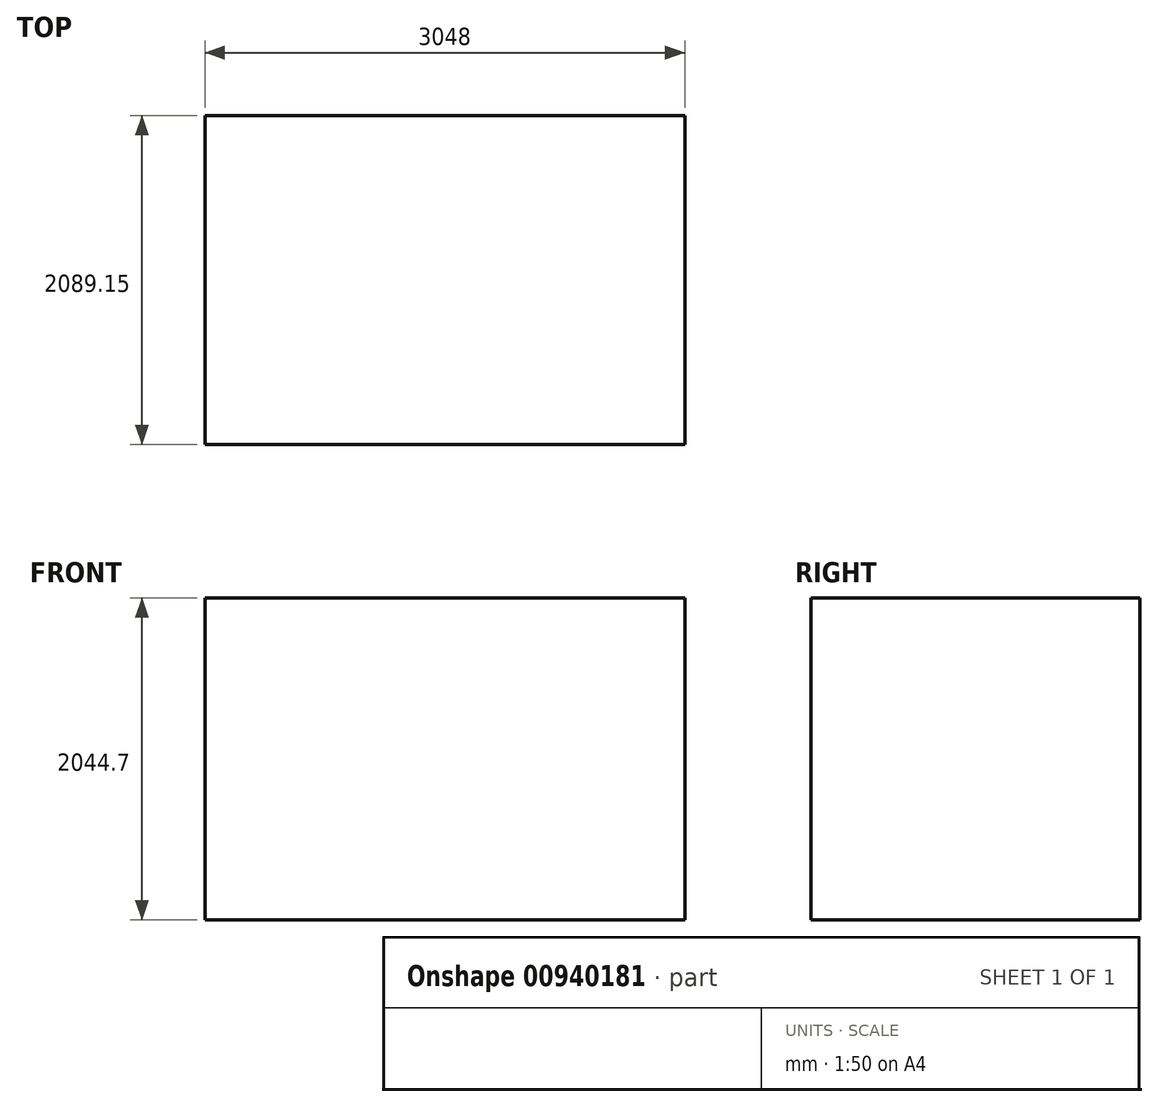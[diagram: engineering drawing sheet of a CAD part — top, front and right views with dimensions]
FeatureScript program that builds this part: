
annotation { "Feature Type Name" : "Feature", "Feature Type Description" : "" }
export const myFeature = defineFeature(function(context is Context, id is Id, definition is map)
    precondition{}
    {
        {
            var Q0;
            Q0=qCreatedBy(makeId("Front.planeOp"),FACE);
            var sketch = newSketch(context, id + "F0", { "sketchPlane" : qUnion([Q0])});
            skLineSegment(sketch, "E0.bottom", {"start": v(-1524, -1022.35) * mm, "end": v(1524, -1022.35) * mm});
            skLineSegment(sketch, "E0.top", {"start": v(-1524, 1022.35) * mm, "end": v(1524, 1022.35) * mm});
            skLineSegment(sketch, "E0.left", {"start": v(-1524, -1022.35) * mm, "end": v(-1524, 1022.35) * mm});
            skLineSegment(sketch, "E0.right", {"start": v(1524, -1022.35) * mm, "end": v(1524, 1022.35) * mm});
            skPoint(sketch, "E0.middle", {"position": v(0, 0) * mm});
            skLineSegment(sketch, "E1.bottom", {"start": v(-1200.05, 668.02) * mm, "end": v(-658.35, 668.02) * mm});
            skLineSegment(sketch, "E1.top", {"start": v(-1200.05, 161.65) * mm, "end": v(-658.35, 161.65) * mm});
            skLineSegment(sketch, "E1.left", {"start": v(-1200.05, 668.02) * mm, "end": v(-1200.05, 161.65) * mm});
            skLineSegment(sketch, "E1.right", {"start": v(-658.35, 668.02) * mm, "end": v(-658.35, 161.65) * mm});
            skLineSegment(sketch, "E2.bottom", {"start": v(478.03, 556.15) * mm, "end": v(1243.47, 556.15) * mm});
            skLineSegment(sketch, "E2.top", {"start": v(478.03, 0) * mm, "end": v(1243.47, 0) * mm});
            skLineSegment(sketch, "E2.left", {"start": v(478.03, 556.15) * mm, "end": v(478.03, 0) * mm});
            skLineSegment(sketch, "E2.right", {"start": v(1243.47, 556.15) * mm, "end": v(1243.47, 0) * mm});
            skLineSegment(sketch, "E3.bottom", {"start": v(354.38, -344.72) * mm, "end": v(1367.12, -344.72) * mm});
            skLineSegment(sketch, "E3.top", {"start": v(354.38, -939.4) * mm, "end": v(1367.12, -939.4) * mm});
            skLineSegment(sketch, "E3.left", {"start": v(354.38, -344.72) * mm, "end": v(354.38, -939.4) * mm});
            skLineSegment(sketch, "E3.right", {"start": v(1367.12, -344.72) * mm, "end": v(1367.12, -939.4) * mm});
            skText(sketch, "E4", { "text": "microwave", "fontName": "OpenSans-Regular.ttf"});
            skPoint(sketch, "E5", {"position": v(860.75, -344.72) * mm});
            skLineSegment(sketch, "E6", {"start": v(860.75, -344.72) * mm, "end": v(860.75, 1191.32) * mm, "construction": true});
            skPoint(sketch, "E7", {"position": v(860.75, 556.15) * mm});
            skText(sketch, "E8", { "text": "back wall", "fontName": "OpenSans-Regular.ttf"});
            skText(sketch, "E9", { "text": "window", "fontName": "OpenSans-Regular.ttf"});
            skText(sketch, "E10", { "text": "oven", "fontName": "OpenSans-Regular.ttf"});
            const initialGuessF0  = {"E4": [0.64839, 0.26293, 1, 0, 0.06366], "E8": [-0.68602, -0.1729, 1, 0, 0.0863], "E9": [-1.08292, 0.38795, 1, 0, 0.07798], "E10": [0.65703, -0.70805, 1, 0, 0.08726]};
            skSetInitialGuess(sketch, initialGuessF0);
            skSolve(sketch);
        }
        {
            var Q0;
            Q0 = qSketchRegion(id + "F0", true);
            var Q1;
            Q1=makeQuery(id+"F0.imprint","IMPRINT",FACE,{"disambiguationData":[TD([[makeQuery(id+"F0.imprint","IMPRINT",EDGE,{"derivedFrom":sQuery(id+"F0.wireOp",EDGE,"E8.sketch_text.stroke-122")}),1.0]])]});
            var Q2;
            Q2=makeQuery(id+"F0.imprint","IMPRINT",FACE,{"disambiguationData":[TD([[makeQuery(id+"F0.imprint","IMPRINT",EDGE,{"derivedFrom":sQuery(id+"F0.wireOp",EDGE,"E8.sketch_text.stroke-65")}),-1.0]])]});
            var Q3;
            Q3=makeQuery(id+"F0.imprint","IMPRINT",FACE,{"disambiguationData":[TD([[makeQuery(id+"F0.imprint","IMPRINT",EDGE,{"derivedFrom":sQuery(id+"F0.wireOp",EDGE,"E8.sketch_text.stroke-80")}),-1.0]])]});
            var Q4;
            Q4=makeQuery(id+"F0.imprint","IMPRINT",FACE,{"disambiguationData":[TD([[makeQuery(id+"F0.imprint","IMPRINT",EDGE,{"derivedFrom":sQuery(id+"F0.wireOp",EDGE,"E4.sketch_text.stroke-77")}),1.0]])]});
            var Q5;
            Q5=makeQuery(id+"F0.imprint","IMPRINT",FACE,{"disambiguationData":[TD([[makeQuery(id+"F0.imprint","IMPRINT",EDGE,{"derivedFrom":sQuery(id+"F0.wireOp",EDGE,"E4.sketch_text.stroke-127")}),1.0]])]});
            var Q6;
            Q6=makeQuery(id+"F0.imprint","IMPRINT",FACE,{"disambiguationData":[TD([[makeQuery(id+"F0.imprint","IMPRINT",EDGE,{"derivedFrom":sQuery(id+"F0.wireOp",EDGE,"E8.sketch_text.stroke-15")}),1.0]])]});
            var Q7;
            Q7=makeQuery(id+"F0.imprint","IMPRINT",FACE,{"disambiguationData":[TD([[makeQuery(id+"F0.imprint","IMPRINT",EDGE,{"derivedFrom":sQuery(id+"F0.wireOp",EDGE,"E8.sketch_text.stroke-42")}),1.0]])]});
            var Q8;
            Q8=makeQuery(id+"F0.imprint","IMPRINT",FACE,{"disambiguationData":[TD([[makeQuery(id+"F0.imprint","IMPRINT",EDGE,{"derivedFrom":sQuery(id+"F0.wireOp",EDGE,"E8.sketch_text.stroke-0")}),-1.0]])]});
            var Q9;
            Q9=makeQuery(id+"F0.imprint","IMPRINT",FACE,{"disambiguationData":[TD([[makeQuery(id+"F0.imprint","IMPRINT",EDGE,{"derivedFrom":sQuery(id+"F0.wireOp",EDGE,"E8.sketch_text.stroke-134")}),-1.0]])]});
            var Q10;
            Q10=makeQuery(id+"F0.imprint","IMPRINT",FACE,{"disambiguationData":[TD([[makeQuery(id+"F0.imprint","IMPRINT",EDGE,{"derivedFrom":sQuery(id+"F0.wireOp",EDGE,"E10.sketch_text.stroke-0")}),-1.0]])]});
            var Q11;
            Q11=makeQuery(id+"F0.imprint","IMPRINT",FACE,{"disambiguationData":[TD([[makeQuery(id+"F0.imprint","IMPRINT",EDGE,{"derivedFrom":sQuery(id+"F0.wireOp",EDGE,"E9.sketch_text.stroke-67")}),1.0]])]});
            var Q12;
            Q12=makeQuery(id+"F0.imprint","IMPRINT",FACE,{"disambiguationData":[TD([[makeQuery(id+"F0.imprint","IMPRINT",EDGE,{"derivedFrom":sQuery(id+"F0.wireOp",EDGE,"E9.sketch_text.stroke-85")}),1.0]])]});
            var Q13;
            Q13=makeQuery(id+"F0.imprint","IMPRINT",FACE,{"disambiguationData":[TD([[makeQuery(id+"F0.imprint","IMPRINT",EDGE,{"derivedFrom":sQuery(id+"F0.wireOp",EDGE,"E3.bottom")}),-1.0]])]});
            var Q14;
            Q14=makeQuery(id+"F0.imprint","IMPRINT",FACE,{"disambiguationData":[TD([[makeQuery(id+"F0.imprint","IMPRINT",EDGE,{"derivedFrom":sQuery(id+"F0.wireOp",EDGE,"E1.bottom")}),-1.0]])]});
            var Q15;
            Q15=makeQuery(id+"F0.imprint","IMPRINT",FACE,{"disambiguationData":[TD([[makeQuery(id+"F0.imprint","IMPRINT",EDGE,{"derivedFrom":sQuery(id+"F0.wireOp",EDGE,"E10.sketch_text.stroke-9")}),1.0]])]});
            var Q16;
            Q16=makeQuery(id+"F0.imprint","IMPRINT",FACE,{"disambiguationData":[TD([[makeQuery(id+"F0.imprint","IMPRINT",EDGE,{"derivedFrom":sQuery(id+"F0.wireOp",EDGE,"E0.bottom")}),1.0]])]});
            var Q17;
            Q17=makeQuery(id+"F0.imprint","IMPRINT",FACE,{"disambiguationData":[TD([[makeQuery(id+"F0.imprint","IMPRINT",EDGE,{"derivedFrom":sQuery(id+"F0.wireOp",EDGE,"E2.bottom")}),-1.0]])]});
            var Q18;
            Q18=makeQuery(id+"F0.imprint","IMPRINT",FACE,{"disambiguationData":[TD([[makeQuery(id+"F0.imprint","IMPRINT",EDGE,{"derivedFrom":sQuery(id+"F0.wireOp",EDGE,"E10.sketch_text.stroke-41")}),1.0]])]});
            var Q19;
            Q19=makeQuery(id+"F0.imprint","IMPRINT",FACE,{"disambiguationData":[TD([[makeQuery(id+"F0.imprint","IMPRINT",EDGE,{"derivedFrom":sQuery(id+"F0.wireOp",EDGE,"E4.sketch_text.stroke-0")}),-1.0]])]});
            var Q20;
            Q20=makeQuery(id+"F0.imprint","IMPRINT",FACE,{"disambiguationData":[TD([[makeQuery(id+"F0.imprint","IMPRINT",EDGE,{"derivedFrom":sQuery(id+"F0.wireOp",EDGE,"E4.sketch_text.stroke-28")}),-1.0]])]});
            var Q21;
            Q21=makeQuery(id+"F0.imprint","IMPRINT",FACE,{"disambiguationData":[TD([[makeQuery(id+"F0.imprint","IMPRINT",EDGE,{"derivedFrom":sQuery(id+"F0.wireOp",EDGE,"E4.sketch_text.stroke-40")}),-1.0]])]});
            var Q22;
            Q22=makeQuery(id+"F0.imprint","IMPRINT",FACE,{"disambiguationData":[TD([[makeQuery(id+"F0.imprint","IMPRINT",EDGE,{"derivedFrom":sQuery(id+"F0.wireOp",EDGE,"E4.sketch_text.stroke-55")}),-1.0]])]});
            var Q23;
            Q23=makeQuery(id+"F0.imprint","IMPRINT",FACE,{"disambiguationData":[TD([[makeQuery(id+"F0.imprint","IMPRINT",EDGE,{"derivedFrom":sQuery(id+"F0.wireOp",EDGE,"E4.sketch_text.stroke-85")}),-1.0]])]});
            var Q24;
            Q24=makeQuery(id+"F0.imprint","IMPRINT",FACE,{"disambiguationData":[TD([[makeQuery(id+"F0.imprint","IMPRINT",EDGE,{"derivedFrom":sQuery(id+"F0.wireOp",EDGE,"E4.sketch_text.stroke-135")}),-1.0]])]});
            var Q25;
            Q25=makeQuery(id+"F0.imprint","IMPRINT",FACE,{"disambiguationData":[TD([[makeQuery(id+"F0.imprint","IMPRINT",EDGE,{"derivedFrom":sQuery(id+"F0.wireOp",EDGE,"E4.sketch_text.stroke-159")}),1.0]])]});
            var Q26;
            Q26=makeQuery(id+"F0.imprint","IMPRINT",FACE,{"disambiguationData":[TD([[makeQuery(id+"F0.imprint","IMPRINT",EDGE,{"derivedFrom":sQuery(id+"F0.wireOp",EDGE,"E8.sketch_text.stroke-50")}),-1.0]])]});
            var Q27;
            Q27=makeQuery(id+"F0.imprint","IMPRINT",FACE,{"disambiguationData":[TD([[makeQuery(id+"F0.imprint","IMPRINT",EDGE,{"derivedFrom":sQuery(id+"F0.wireOp",EDGE,"E4.sketch_text.stroke-145")}),-1.0]])]});
            var Q28;
            Q28=makeQuery(id+"F0.imprint","IMPRINT",FACE,{"disambiguationData":[TD([[makeQuery(id+"F0.imprint","IMPRINT",EDGE,{"derivedFrom":sQuery(id+"F0.wireOp",EDGE,"E4.sketch_text.stroke-68")}),-1.0]])]});
            var Q29;
            Q29=makeQuery(id+"F0.imprint","IMPRINT",FACE,{"disambiguationData":[TD([[makeQuery(id+"F0.imprint","IMPRINT",EDGE,{"derivedFrom":sQuery(id+"F0.wireOp",EDGE,"E4.sketch_text.stroke-108")}),-1.0]])]});
            var Q30;
            Q30=makeQuery(id+"F0.imprint","IMPRINT",FACE,{"disambiguationData":[TD([[makeQuery(id+"F0.imprint","IMPRINT",EDGE,{"derivedFrom":sQuery(id+"F0.wireOp",EDGE,"E8.sketch_text.stroke-130")}),-1.0]])]});
            var Q31;
            Q31=makeQuery(id+"F0.imprint","IMPRINT",FACE,{"disambiguationData":[TD([[makeQuery(id+"F0.imprint","IMPRINT",EDGE,{"derivedFrom":sQuery(id+"F0.wireOp",EDGE,"E8.sketch_text.stroke-23")}),-1.0]])]});
            var Q32;
            Q32=makeQuery(id+"F0.imprint","IMPRINT",FACE,{"disambiguationData":[TD([[makeQuery(id+"F0.imprint","IMPRINT",EDGE,{"derivedFrom":sQuery(id+"F0.wireOp",EDGE,"E9.sketch_text.stroke-0")}),-1.0]])]});
            var Q33;
            Q33=makeQuery(id+"F0.imprint","IMPRINT",FACE,{"disambiguationData":[TD([[makeQuery(id+"F0.imprint","IMPRINT",EDGE,{"derivedFrom":sQuery(id+"F0.wireOp",EDGE,"E8.sketch_text.stroke-103")}),-1.0]])]});
            var Q34;
            Q34=makeQuery(id+"F0.imprint","IMPRINT",FACE,{"disambiguationData":[TD([[makeQuery(id+"F0.imprint","IMPRINT",EDGE,{"derivedFrom":sQuery(id+"F0.wireOp",EDGE,"E9.sketch_text.stroke-23")}),-1.0]])]});
            var Q35;
            Q35=makeQuery(id+"F0.imprint","IMPRINT",FACE,{"disambiguationData":[TD([[makeQuery(id+"F0.imprint","IMPRINT",EDGE,{"derivedFrom":sQuery(id+"F0.wireOp",EDGE,"E9.sketch_text.stroke-52")}),-1.0]])]});
            var Q36;
            Q36=makeQuery(id+"F0.imprint","IMPRINT",FACE,{"disambiguationData":[TD([[makeQuery(id+"F0.imprint","IMPRINT",EDGE,{"derivedFrom":sQuery(id+"F0.wireOp",EDGE,"E9.sketch_text.stroke-27")}),-1.0]])]});
            var Q37;
            Q37=makeQuery(id+"F0.imprint","IMPRINT",FACE,{"disambiguationData":[TD([[makeQuery(id+"F0.imprint","IMPRINT",EDGE,{"derivedFrom":sQuery(id+"F0.wireOp",EDGE,"E9.sketch_text.stroke-76")}),-1.0]])]});
            var Q38;
            Q38=makeQuery(id+"F0.imprint","IMPRINT",FACE,{"disambiguationData":[TD([[makeQuery(id+"F0.imprint","IMPRINT",EDGE,{"derivedFrom":sQuery(id+"F0.wireOp",EDGE,"E9.sketch_text.stroke-35")}),-1.0]])]});
            var Q39;
            Q39=makeQuery(id+"F0.imprint","IMPRINT",FACE,{"disambiguationData":[TD([[makeQuery(id+"F0.imprint","IMPRINT",EDGE,{"derivedFrom":sQuery(id+"F0.wireOp",EDGE,"E10.sketch_text.stroke-27")}),-1.0]])]});
            var Q40;
            Q40=makeQuery(id+"F0.imprint","IMPRINT",FACE,{"disambiguationData":[TD([[makeQuery(id+"F0.imprint","IMPRINT",EDGE,{"derivedFrom":sQuery(id+"F0.wireOp",EDGE,"E9.sketch_text.stroke-93")}),-1.0]])]});
            var Q41;
            Q41=makeQuery(id+"F0.imprint","IMPRINT",FACE,{"disambiguationData":[TD([[makeQuery(id+"F0.imprint","IMPRINT",EDGE,{"derivedFrom":sQuery(id+"F0.wireOp",EDGE,"E10.sketch_text.stroke-17")}),-1.0]])]});
            var Q42;
            Q42=makeQuery(id+"F0.imprint","IMPRINT",FACE,{"disambiguationData":[TD([[makeQuery(id+"F0.imprint","IMPRINT",EDGE,{"derivedFrom":sQuery(id+"F0.wireOp",EDGE,"E10.sketch_text.stroke-46")}),-1.0]])]});
            var Q43;
            Q43=makeQuery(id+"F0.imprint","IMPRINT",FACE,{"disambiguationData":[TD([[makeQuery(id+"F0.imprint","IMPRINT",EDGE,{"derivedFrom":sQuery(id+"F0.wireOp",EDGE,"E4.sketch_text.stroke-32")}),-1.0]])]});
            var Q44;
            Q44=sQuery(id+"F0.wireOp",EDGE,"E0.left");
            var Q45;
            Q45=sQuery(id+"F0.wireOp",EDGE,"E0.right");
            var Q46;
            Q46=sQuery(id+"F0.wireOp",EDGE,"E0.bottom");
            extrude(context, id + "F1", {"entities" : qUnion([Q0, Q1, Q2, Q3, Q4, Q5, Q6, Q7, Q8, Q9, Q10, Q11, Q12, Q13, Q14, Q15, Q16, Q17, Q18, Q19, Q20, Q21, Q22, Q23, Q24, Q25, Q26, Q27, Q28, Q29, Q30, Q31, Q32, Q33, Q34, Q35, Q36, Q37, Q38, Q39, Q40, Q41, Q42, Q43]), "bodyType" : ToolBodyType.SURFACE, "surfaceEntities" : qUnion([Q44, Q45, Q46]), "depth" : 2089.15 * mm, "offsetDistance" : 25.4 * mm});
        }
        {
            var Q0;
            Q0=makeQuery(id+"F1.opExtrude","SWEPT_FACE",FACE,{"disambiguationData":[OSD([sQuery(id+"F0.wireOp",EDGE,"E0.left")])]});
            var sketch = newSketch(context, id + "F2", { "sketchPlane" : qUnion([Q0])});
            skLineSegment(sketch, "E11", {"start": v(0, 1022.35) * mm, "end": v(0, -1022.35) * mm});
            skLineSegment(sketch, "E12", {"start": v(2089.15, 1022.35) * mm, "end": v(2089.15, -1022.35) * mm});
            skSolve(sketch);
        }
        {
            var Q0;
            Q0=sQuery(id+"F2.wireOp",EDGE,"E11");
            var Q1;
            Q1=sQuery(id+"F2.wireOp",EDGE,"E12");
            extrude(context, id + "F3", {"bodyType" : ToolBodyType.SURFACE, "surfaceEntities" : qUnion([Q0, Q1]), "oppositeDirection" : true, "depth" : 3048 * mm, "offsetDistance" : 25.4 * mm});
        }
    });
